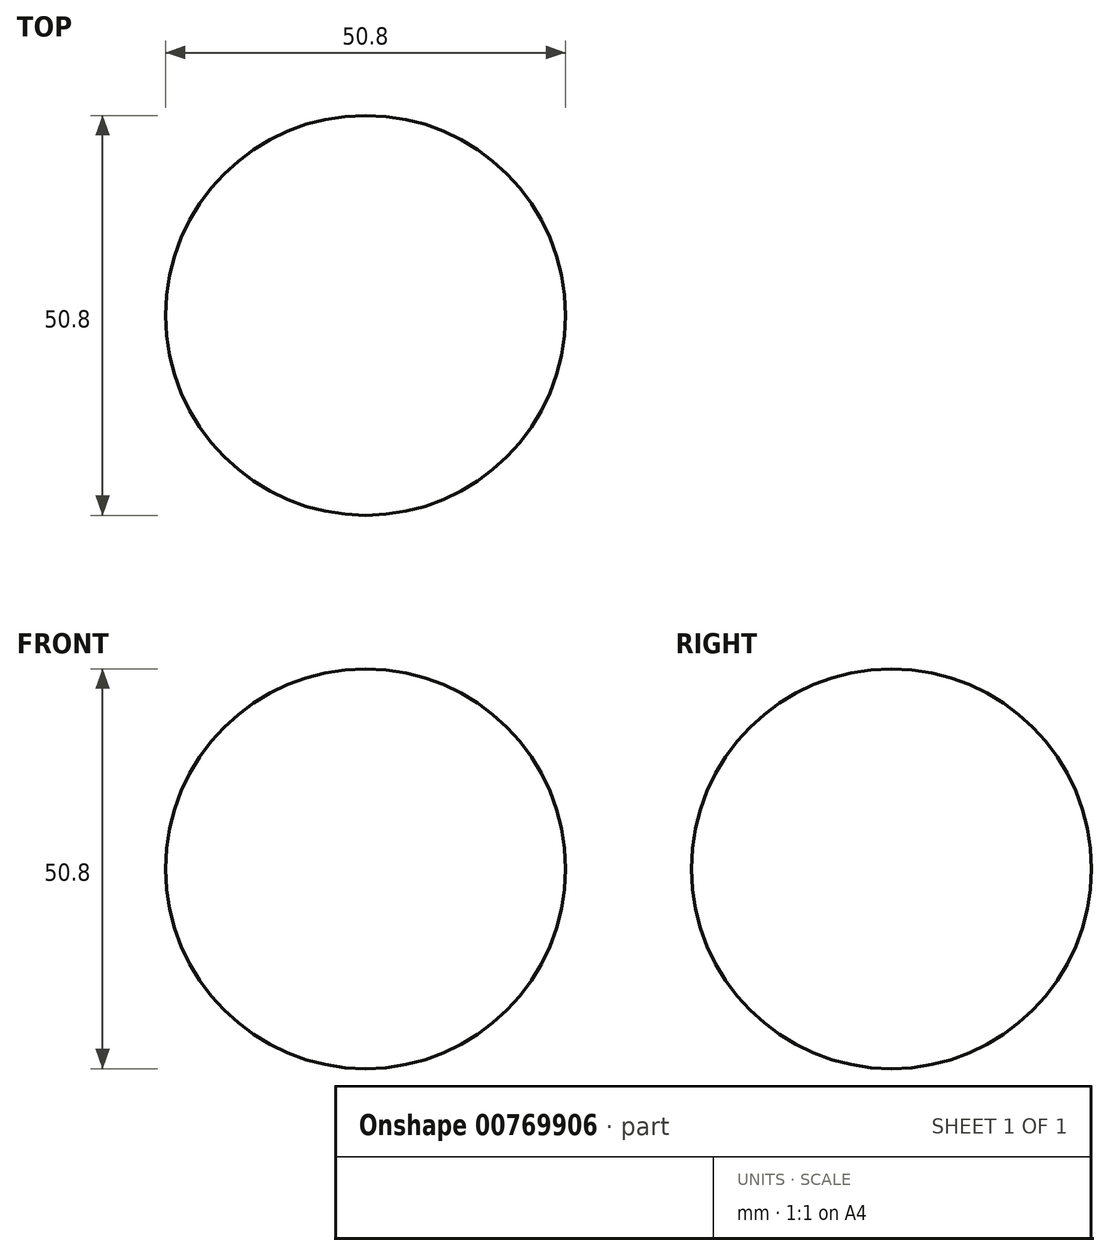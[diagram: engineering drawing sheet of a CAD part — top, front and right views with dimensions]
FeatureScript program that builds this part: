
annotation { "Feature Type Name" : "Feature", "Feature Type Description" : "" }
export const myFeature = defineFeature(function(context is Context, id is Id, definition is map)
    precondition{}
    {
        {
            var Q0;
            Q0=qCreatedBy(makeId("Front.planeOp"),FACE);
            var sketch = newSketch(context, id + "F0", { "sketchPlane" : qUnion([Q0])});
            skLineSegment(sketch, "E0", {"start": v(0, 0) * mm, "end": v(0, 50.8) * mm});
            skArc(sketch, "E1", {"start": v(0, 0) * mm, "mid": v(25.4, 25.4) * mm, "end": v(0, 50.8) * mm});
            skSolve(sketch);
        }
        {
            var Q0;
            Q0=sQuery(id+"F0.wireOp",EDGE,"E1");
            var Q1;
            Q1=sQuery(id+"F0.wireOp",EDGE,"E1");
            var Q2;
            Q2=sQuery(id+"F0.wireOp",EDGE,"E0");
            revolve(context, id + "F1", {"bodyType" : ToolBodyType.SURFACE, "surfaceOperationType" : NewSurfaceOperationType.NEW, "surfaceEntities" : qUnion([Q0, Q1]), "axis" : qUnion([Q2]), "revolveType" : RevolveType.FULL});
        }
    });
